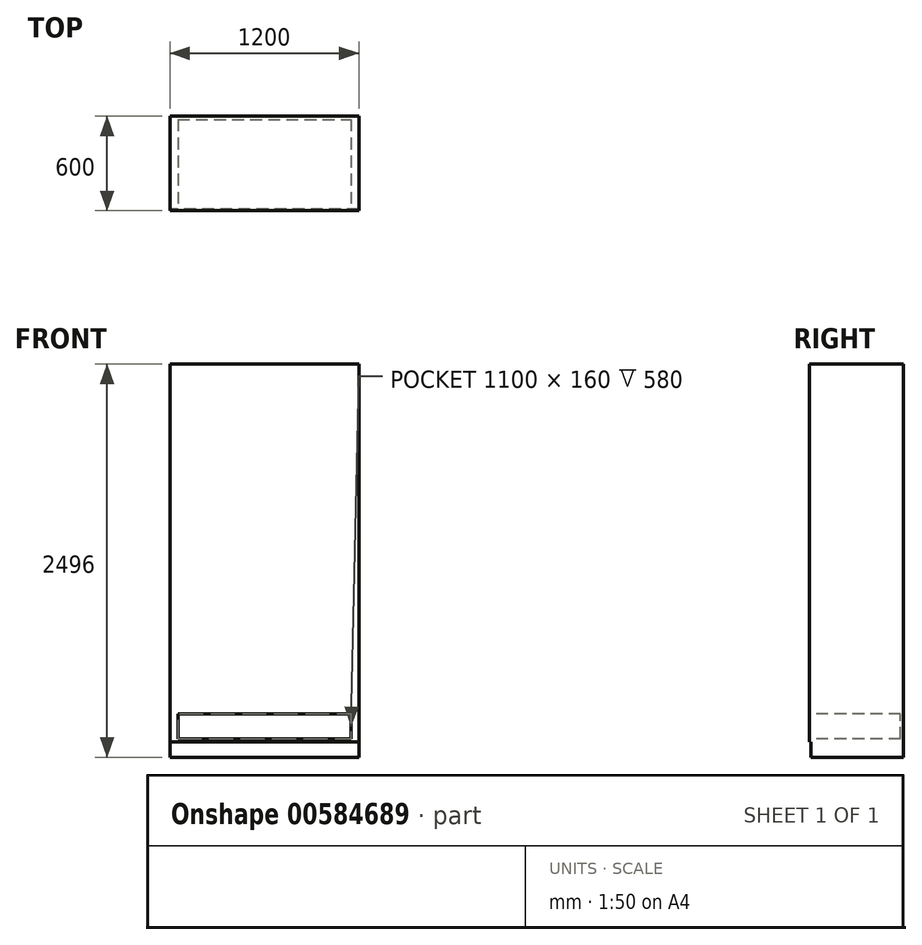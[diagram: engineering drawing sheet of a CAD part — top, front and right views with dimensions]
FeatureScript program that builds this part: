
annotation { "Feature Type Name" : "Feature", "Feature Type Description" : "" }
export const myFeature = defineFeature(function(context is Context, id is Id, definition is map)
    precondition{}
    {
        {
            var Q0;
            Q0=qCreatedBy(makeId("Right.planeOp"),FACE);
            var sketch = newSketch(context, id + "F0", { "sketchPlane" : qUnion([Q0])});
            skLineSegment(sketch, "E0.bottom", {"start": v(300, -1248) * mm, "end": v(-300, -1248) * mm});
            skLineSegment(sketch, "E0.top", {"start": v(300, 1248) * mm, "end": v(-300, 1248) * mm});
            skLineSegment(sketch, "E0.left", {"start": v(300, -1248) * mm, "end": v(300, 1248) * mm});
            skLineSegment(sketch, "E0.right", {"start": v(-300, -1248) * mm, "end": v(-300, 1248) * mm});
            skPoint(sketch, "E0.middle", {"position": v(0, 0) * mm});
            skSolve(sketch);
        }
        {
            var Q0;
            Q0 = qSketchRegion(id + "F0", true);
            extrude(context, id + "F1", {"entities" : qUnion([Q0]), "depth" : 1200 * mm, "offsetDistance" : 25 * mm});
        }
        {
            var Q0;
            Q0=makeQuery(id+"F1.opExtrude","SWEPT_FACE",FACE,{"disambiguationData":[OSD([sQuery(id+"F0.wireOp",EDGE,"E0.right")])]});
            var sketch = newSketch(context, id + "F2", { "sketchPlane" : qUnion([Q0])});
            skLineSegment(sketch, "E1.bottom", {"start": v(0, -1248) * mm, "end": v(1200, -1248) * mm});
            skLineSegment(sketch, "E1.top", {"start": v(0, -1152) * mm, "end": v(1200, -1152) * mm});
            skLineSegment(sketch, "E1.left", {"start": v(0, -1248) * mm, "end": v(0, -1152) * mm});
            skLineSegment(sketch, "E1.right", {"start": v(1200, -1248) * mm, "end": v(1200, -1152) * mm});
            skSolve(sketch);
        }
        {
            var Q0;
            Q0 = qSketchRegion(id + "F2", true);
            extrude(context, id + "F3", {"entities" : qUnion([Q0]), "operationType" : NewBodyOperationType.REMOVE, "oppositeDirection" : true, "depth" : 10 * mm, "offsetDistance" : 25 * mm});
        }
        {
            var Q0;
            Q0=makeQuery(id+"F1.opExtrude","SWEPT_FACE",FACE,{"disambiguationData":[OSD([sQuery(id+"F0.wireOp",EDGE,"E0.right")])]});
            var sketch = newSketch(context, id + "F4", { "sketchPlane" : qUnion([Q0])});
            skLineSegment(sketch, "E2.bottom", {"start": v(0, -1152) * mm, "end": v(1200, -1152) * mm});
            skLineSegment(sketch, "E2.top", {"start": v(0, -952) * mm, "end": v(1200, -952) * mm});
            skLineSegment(sketch, "E2.left", {"start": v(0, -1152) * mm, "end": v(0, -952) * mm});
            skLineSegment(sketch, "E2.right", {"start": v(1200, -1152) * mm, "end": v(1200, -952) * mm});
            skLineSegment(sketch, "E3.bottom", {"start": v(50, -1132) * mm, "end": v(1150, -1132) * mm});
            skLineSegment(sketch, "E3.top", {"start": v(50, -972) * mm, "end": v(1150, -972) * mm});
            skLineSegment(sketch, "E3.left", {"start": v(50, -1132) * mm, "end": v(50, -972) * mm});
            skLineSegment(sketch, "E3.right", {"start": v(1150, -1132) * mm, "end": v(1150, -972) * mm});
            skSolve(sketch);
        }
        {
            var Q0;
            Q0=makeQuery(id+"F4.imprint","IMPRINT",FACE,{"disambiguationData":[TD([[makeQuery(id+"F4.imprint","IMPRINT",EDGE,{"derivedFrom":sQuery(id+"F4.wireOp",EDGE,"E3.bottom")}),1.0]])]});
            extrude(context, id + "F5", {"entities" : qUnion([Q0]), "operationType" : NewBodyOperationType.REMOVE, "oppositeDirection" : true, "depth" : 580 * mm, "offsetDistance" : 25 * mm});
        }
    });
